# Revit family: METEOR_Atria II 4_REVIT_File (Standard)
name_source: partatom
category: Lighting Fixtures
revit_build: Autodesk Revit 2017 (Build: 20160225_1515(x64)
units: mm (PartAtom-declared; Revit-internal decimal feet)

## family parameters
Always vertical = Yes
Cut with Voids When Loaded = No
Light Source = Yes
OmniClass Number = 23.80.70.00
OmniClass Title = Lighting
Part Type = Normal
Room Calculation Point = No
Round Connector Dimension = Use Diameter
Shared = No
Work Plane-Based = Yes

## types (100) — shared parameters
Color Filter = 16777215
Default Elevation = 4' - 0"
Dimming Lamp Color Temperature Shift = <None>
StemLength = 2' - 0"
Tilt Angle = 90.00°

## per-type parameters (varying)
| type | Lamp | Photometric Web File | Wattage Comments |
| ASII4-15W-278-20D | ASII4-15W-278-20D | AS4-15-278-XXX-XXX-20-XXX-XXX.ies | 15 |
| ASII4-15W-278-35D | ASII4-15W-278-20D | AS4-15-278-XXX-XXX-35-XXX-XXX.ies | 15 |
| ASII4-15W-278-45D | ASII4-15W-278-45D | ASII4-15-278-XXX-XXX-45-XXX-XXX.ies | 15 |
| ASII4-15W-278-55D | ASII4-15W-278-55D | ASII4-15-278-XXX-XXX-55-XXX-XXX.ies | 15 |
| ASII4-15W-278-WD | ASII4-15W-278-WD | ASII4-15-278-XXX-XXX-WD-XXX-XXX-DF.ies | 15 |
| ASII4-15W-308-20D | ASII4-15W-308-20D | ASII4-15-308-XXX-XXX-20-XXX-XXX.ies | 15 |
| ASII4-15W-308-35D | ASII4-15W-308-35D | ASII4-15-308-XXX-XXX-35-XXX-XXX.ies | 15 |
| ASII4-15W-308-45D | ASII4-15W-308-45D | ASII4-15-308-XXX-XXX-45-XXX-XXX.ies | 15 |
| ASII4-15W-308-55D | ASII4-15W-308-55D | ASII4-15-308-XXX-XXX-55-XXX-XXX.ies | 15 |
| ASII4-15W-308-WD | ASII4-15W-308-WD | ASII4-15-308-XXX-XXX-WD-XXX-XXX-DF.ies | 15 |
| ASII4-15W-358-20D | ASII4-15W-358-20D | ASII4-15-358-XXX-XXX-20-XXX-XXX.ies | 15 |
| ASII4-15W-408-WD | ASII4-15W-408-WD | ASII4-15-408-XXX-XXX-WD-XXX-XXX-DF.ies | 15 |
| ASII4-25W-408-WD | ASII4-25W-408-WD | ASII4-25-408-XXX-XXX-WD-XXX-XXX-DF.ies | 25 |
| ASII4-25W-408-55D | ASII4-25W-408-55D | ASII4-25-408-XXX-XXX-55-XXX-XXX.ies | 25 |
| ASII4-25W-408-45D | ASII4-25W-408-45D | ASII4-25-408-XXX-XXX-45-XXX-XXX.ies | 25 |
| ASII4-25W-408-35D | ASII4-25W-408-35D | ASII4-25-408-XXX-XXX-35-XXX-XXX.ies | 25 |
| ASII4-25W-408-20D | ASII4-25W-408-20D | ASII4-25-408-XXX-XXX-20-XXX-XXX.ies | 25 |
| ASII4-25W-358-20D | ASII4-25W-358-20D | ASII4-25-358-XXX-XXX-20-XXX-XXX.ies | 25 |
| ASII4-25W-358-35D | ASII4-25W-358-35D | ASII4-25-358-XXX-XXX-35-XXX-XXX.ies | 25 |
| ASII4-25W-358-45D | ASII4-25W-358-45D | ASII4-25-358-XXX-XXX-45-XXX-XXX.ies | 25 |
| ASII4-25W-358-55D | ASII4-25W-358-55D | ASII4-25-358-XXX-XXX-55-XXX-XXX.ies | 25 |
| ASII4-25W-308-20D | ASII4-25W-308-20D | ASII4-25-308-XXX-XXX-20-XXX-XXX.ies | 25 |
| ASII4-25W-308-35D | ASII4-25W-308-35D | ASII4-25-308-XXX-XXX-35-XXX-XXX.ies | 25 |
| ASII4-25W-308-45D | ASII4-25W-308-45D | ASII4-25-308-XXX-XXX-45-XXX-XXX.ies | 25 |
| ASII4-25W-308-55D | ASII4-25W-308-55D | ASII4-25-308-XXX-XXX-55-XXX-XXX.ies | 25 |
| ASII4-25W-308-WD | ASII4-25W-308-WD | ASII4-25-308-XXX-XXX-55-XXX-XXX.ies | 25 |
| ASII4-25W-358-WD | ASII4-25W-358-WD | ASII4-25-358-XXX-XXX-WD-XXX-XXX-DF.ies | 25 |
| ASII4-15W-358-45D | ASII4-15W-358-45D | ASII4-15-358-XXX-XXX-45-XXX-XXX.ies | 15 |
| ASII4-15W-358-55D | ASII4-15W-358-55D | ASII4-15-358-XXX-XXX-55-XXX-XXX.ies | 15 |
| ASII4-15W-358-WD | ASII4-15W-358-55D | ASII4-15-358-XXX-XXX-WD-XXX-XXX-DF.ies | 15 |
| ASII4-15W-358-35D | ASII4-15W-358-35D | ASII4-15-358-XXX-XXX-35-XXX-XXX.ies | 15 |
| ASII4-15W-408-55D | ASII4-15W-408-55D | ASII4-15-408-XXX-XXX-55-XXX-XXX.ies | 15 |
| ASII4-15W-408-45D | ASII4-15W-408-45D | ASII4-15-408-XXX-XXX-45-XXX-XXX.ies | 15 |
| ASII4-15W-408-35D | ASII4-15W-408-35D | ASII4-15-408-XXX-XXX-35-XXX-XXX.ies | 15 |
| ASII4-15W-408-20D | ASII4-15W-408-20D | ASII4-15-408-XXX-XXX-20-XXX-XXX.ies | 15 |
| ASII4-25W-278-20D | ASII4-25W-278-20D | ASII4-25-278-XXX-XXX-20-XXX-XXX.ies | 25 |
| ASII4-25W-278-35D | ASII4-25W-278-35D | ASII4-25-278-XXX-XXX-35-XXX-XXX.ies | 25 |
| ASII4-25W-278-45D | ASII4-25W-278-45D | ASII4-25-278-XXX-XXX-45-XXX-XXX.ies | 25 |
| ASII4-25W-278-55D | ASII4-25W-278-55D | ASII4-25-278-XXX-XXX-55-XXX-XXX.ies | 25 |
| ASII4-25W-278-WD | ASII4-25W-278-WD | ASII4-25-278-XXX-XXX-WD-XXX-XXX-DF.ies | 25 |
| ASII4-35W-278-20D | ASII4-35W-278-20D | ASII4-35-278-XXX-XXX-20-XXX-XXX.ies | 35 |
| ASII4-35W-278-35D | ASII4-35W-278-35D | ASII4-35-278-XXX-XXX-35-XXX-XXX.ies | 35 |
| ASII4-35W-278-45D | ASII4-35W-278-45D | ASII4-35-278-XXX-XXX-45-XXX-XXX.ies | 35 |
| ASII4-35W-278-55D | ASII4-35W-278-55D | ASII4-35-278-XXX-XXX-55-XXX-XXX.ies | 35 |
| ASII4-35W-278-WD | ASII4-35W-278-WD | ASII4-35-278-XXX-XXX-WD-XXX-XXX-DF.ies | 35 |
| ASII4-35W-308-20D | ASII4-35W-308-20D | ASII4-35-308-XXX-XXX-20-XXX-XXX.ies | 35 |
| ASII4-35W-308-35D | ASII4-35W-308-35D | ASII4-35-308-XXX-XXX-35-XXX-XXX.ies | 35 |
| ASII4-35W-308-45D | ASII4-35W-308-45D | ASII4-35-308-XXX-XXX-45-XXX-XXX.ies | 35 |
| ASII4-35W-308-55D | ASII4-35W-308-55D | ASII4-35-308-XXX-XXX-55-XXX-XXX.ies | 35 |
| ASII4-35W-308-WD | ASII4-35W-308-WD | ASII4-35-308-XXX-XXX-WD-XXX-XXX-DF.ies | 35 |
| ASII4-35W-358-20D | ASII4-35W-358-20D | ASII4-35-358-XXX-XXX-20-XXX-XXX.ies | 35 |
| ASII4-35W-358-35D | ASII4-35W-358-35D | ASII4-35-358-XXX-XXX-35-XXX-XXX.ies | 35 |
| ASII4-35W-358-45D | ASII4-35W-358-45D | ASII4-35-358-XXX-XXX-45-XXX-XXX.ies | 35 |
| ASII4-35W-358-55D | ASII4-35W-358-55D | ASII4-35-358-XXX-XXX-55-XXX-XXX.ies | 35 |
| ASII4-35W-358-WD | ASII4-35W-358-WD | ASII4-35-358-XXX-XXX-WD-XXX-XXX-DF.ies | 35 |
| ASII4-35W-408-20D | ASII4-35W-408-20D | ASII4-35-408-XXX-XXX-20-XXX-XXX.ies | 35 |
| ASII4-35W-408-35D | ASII4-35W-408-35D | ASII4-35-408-XXX-XXX-35-XXX-XXX.ies | 35 |
| ASII4-35W-408-45D | ASII4-35W-408-45D | ASII4-35-408-XXX-XXX-45-XXX-XXX.ies | 35 |
| ASII4-35W-408-55D | ASII4-35W-408-55D | ASII4-35-408-XXX-XXX-55-XXX-XXX.ies | 35 |
| ASII4-35W-408-WD | ASII4-35W-408-WD | ASII4-35-408-XXX-XXX-WD-XXX-XXX-DF.ies | 35 |
| ASII4-45W-278-20D | ASII4-45W-278-20D | ASII4-45-278-XXX-XXX-20-XXX-XXX.ies | 45 |
| ASII4-45W-278-35D | ASII4-45W-278-35D | ASII4-45-278-XXX-XXX-35-XXX-XXX.ies | 45 |
| ASII4-45W-278-45D | ASII4-45W-278-45D | ASII4-45-278-XXX-XXX-45-XXX-XXX.ies | 45 |
| ASII4-45W-278-55D | ASII4-45W-278-55D | ASII4-45-278-XXX-XXX-55-XXX-XXX.ies | 45 |
| ASII4-45W-278-WD | ASII4-45W-278-WD | ASII4-45-278-XXX-XXX-WD-XXX-XXX-DF.ies | 45 |
| ASII4-45W-308-20D | ASII4-45W-308-20D | ASII4-45-308-XXX-XXX-20-XXX-XXX.ies | 45 |
| ASII4-45W-308-35D | ASII4-45W-308-35D | ASII4-45-308-XXX-XXX-35-XXX-XXX.ies | 45 |
| ASII4-45W-308-45D | ASII4-45W-308-45D | ASII4-45-308-XXX-XXX-45-XXX-XXX.ies | 45 |
| ASII4-45W-308-55D | ASII4-45W-308-55D | ASII4-45-308-XXX-XXX-55-XXX-XXX.ies | 45 |
| ASII4-45W-308-WD | ASII4-45W-308-WD | ASII4-45-308-XXX-XXX-WD-XXX-XXX-DF.ies | 45 |
| ASII4-45W-358-20D | ASII4-45W-358-20D | ASII4-45-308-XXX-XXX-20-XXX-XXX.ies | 45 |
| ASII4-45W-358-35D | ASII4-45W-358-35D | ASII4-45-358-XXX-XXX-35-XXX-XXX.ies | 45 |
| ASII4-45W-358-45D | ASII4-45W-358-45D | ASII4-45-358-XXX-XXX-45-XXX-XXX.ies | 45 |
| ASII4-45W-358-55D | ASII4-45W-358-55D | ASII4-45-358-XXX-XXX-55-XXX-XXX.ies | 45 |
| ASII4-45W-358-WD | ASII4-45W-358-WD | ASII4-45-358-XXX-XXX-WD-XXX-XXX-DF.ies | 45 |
| ASII4-45W-408-20D | ASII4-45W-408-20D | ASII4-45-408-XXX-XXX-20-XXX-XXX.ies | 45 |
| ASII4-45W-408-35D | ASII4-45W-408-35D | ASII4-45-408-XXX-XXX-35-XXX-XXX.ies | 45 |
| ASII4-45W-408-45D | ASII4-45W-408-45D | ASII4-45-408-XXX-XXX-45-XXX-XXX.ies | 45 |
| ASII4-45W-408-55D | ASII4-45W-408-55D | ASII4-45-408-XXX-XXX-55-XXX-XXX.ies | 45 |
| ASII4-45W-408-WD | ASII4-45W-408-WD | ASII4-45-408-XXX-XXX-WD-XXX-XXX-DF.ies | 45 |
| ASII4-65W-278-20D | ASII4-65W-278-20D | ASII4-65-278-XXX-XXX-20-XXX-XXX.ies | 65 |
| ASII4-65W-278-35D | ASII4-65W-278-35D | ASII4-65-278-XXX-XXX-35-XXX-XXX.ies | 65 |
| ASII4-65W-278-45D | ASII4-65W-278-45D | ASII4-65-278-XXX-XXX-45-XXX-XXX.ies | 65 |
| ASII4-65W-278-55D | ASII4-65W-278-55D | ASII4-65-278-XXX-XXX-WD-XXX-XXX-DF.ies | 65 |
| ASII4-65W-278-WD | ASII4-65W-278-WD | ASII4-65-278-XXX-XXX-WD-XXX-XXX-DF.ies | 65 |
| ASII4-65W-308-20D | ASII4-65W-308-20D | ASII4-65-308-XXX-XXX-20-XXX-XXX.ies | 65 |
| ASII4-65W-308-35D | ASII4-65W-308-35D | ASII4-65-308-XXX-XXX-35-XXX-XXX.ies | 65 |
| ASII4-65W-308-45D | ASII4-65W-308-45D | ASII4-65-308-XXX-XXX-45-XXX-XXX.ies | 65 |
| ASII4-65W-308-55D | ASII4-65W-308-55D | ASII4-65-308-XXX-XXX-55-XXX-XXX.ies | 65 |
| ASII4-65W-308-WD | ASII4-65W-308-WD | ASII4-65-308-XXX-XXX-WD-XXX-XXX-DF.ies | 65 |
| ASII4-65W-358-20D | ASII4-65W-358-20D | ASII4-65-358-XXX-XXX-20-XXX-XXX.ies | 65 |
| ASII4-65W-358-35D | ASII4-65W-358-35D | ASII4-65-358-XXX-XXX-35-XXX-XXX.ies | 65 |
| ASII4-65W-358-45D | ASII4-65W-358-45D | ASII4-65-358-XXX-XXX-45-XXX-XXX.ies | 65 |
| ASII4-65W-358-55D | ASII4-65W-358-55D | ASII4-65-358-XXX-XXX-55-XXX-XXX.ies | 65 |
| ASII4-65W-358-WD | ASII4-65W-358-WD | ASII4-65-358-XXX-XXX-WD-XXX-XXX-DF.ies | 65 |
| ASII4-65W-408-20D | ASII4-65W-408-20D | ASII4-65-408-XXX-XXX-20-XXX-XXX.ies | 65 |
| ASII4-65W-408-35D | ASII4-65W-408-35D | ASII4-65-408-XXX-XXX-35-XXX-XXX.ies | 65 |
| ASII4-65W-408-45D | ASII4-65W-408-45D | ASII4-65-408-XXX-XXX-45-XXX-XXX.ies | 65 |
| ASII4-65W-408-55D | ASII4-65W-408-55D | ASII4-65-408-XXX-XXX-55-XXX-XXX.ies | 65 |
| ASII4-65W-408-WD | ASII4-65W-408-WD | ASII4-65-408-XXX-XXX-WD-XXX-XXX-DF.ies | 65 |

## geometry (parser evidence)
native form markers: Sweep x2
no freeform markers — native parametric forms only
